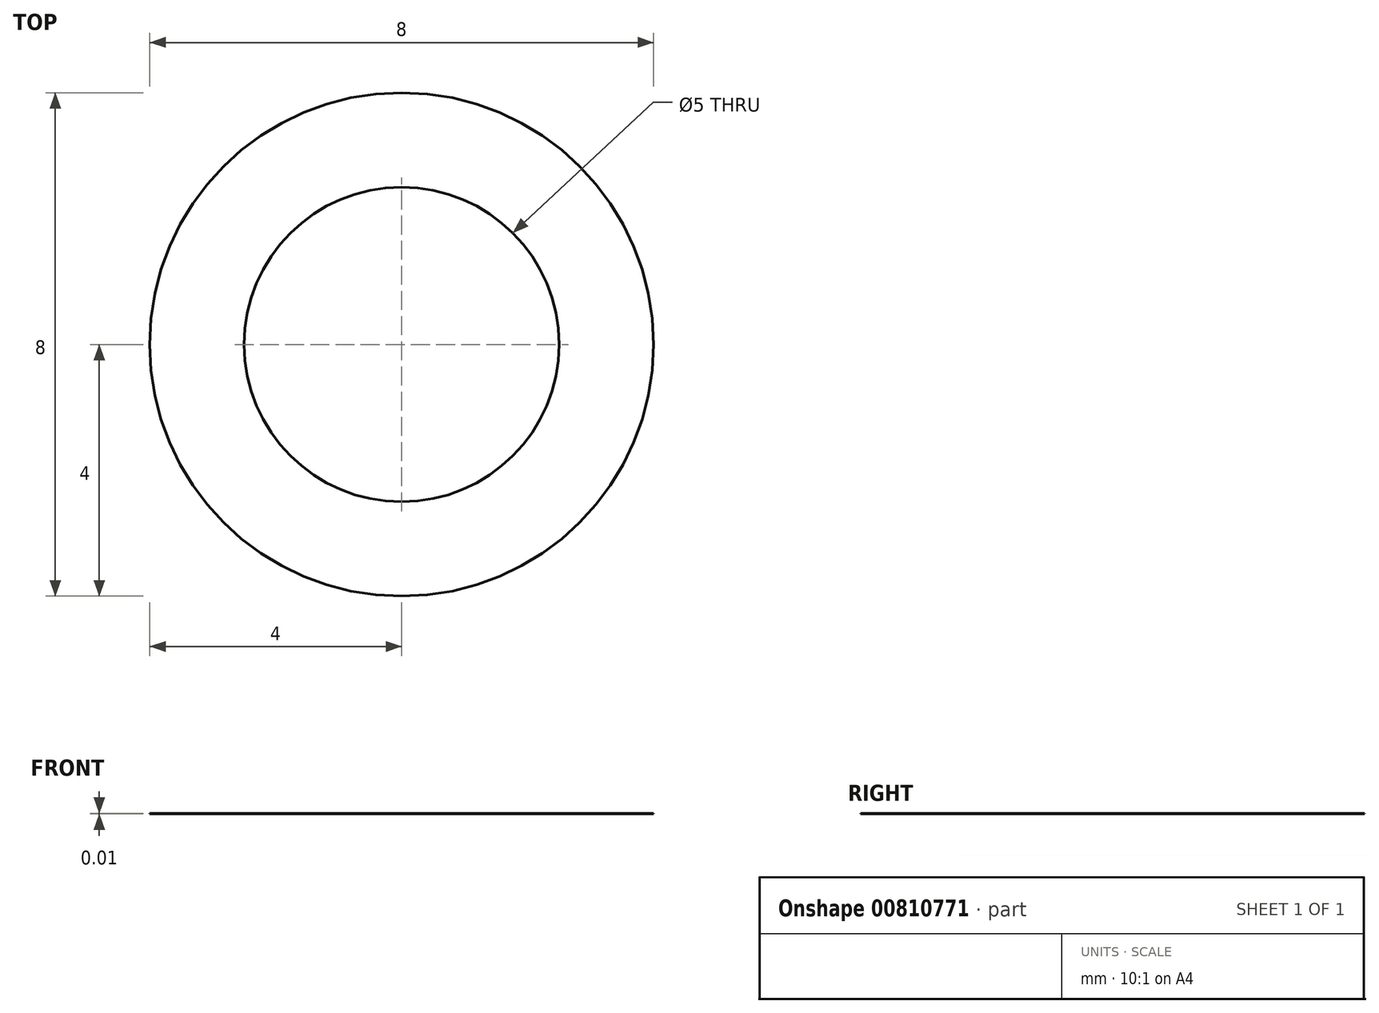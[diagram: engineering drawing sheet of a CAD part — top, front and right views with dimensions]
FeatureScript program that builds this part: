
annotation { "Feature Type Name" : "Feature", "Feature Type Description" : "" }
export const myFeature = defineFeature(function(context is Context, id is Id, definition is map)
    precondition{}
    {
        {
            var Q0;
            Q0=qCreatedBy(makeId("Top.planeOp"),FACE);
            var sketch = newSketch(context, id + "F0", { "sketchPlane" : qUnion([Q0])});
            skCircle(sketch, "E0", {"center": v(0, 0) * mm, "radius": 4 * mm});
            skCircle(sketch, "E1", {"center": v(0, 0) * mm, "radius": 2.5 * mm});
            skSolve(sketch);
        }
        {
            var Q0;
            Q0=qSketchRegion(id+"F0",true);
            extrude(context, id + "F1", {"entities" : qUnion([Q0]), "depth" : 1 / 101.6 * mm});
        }
    });
